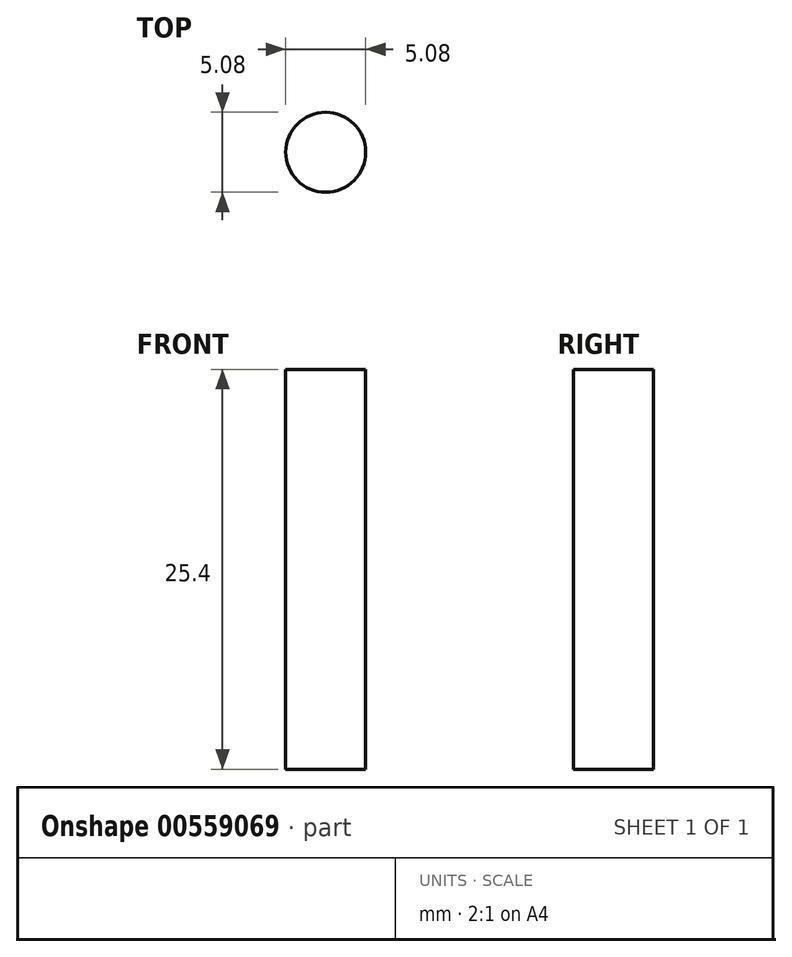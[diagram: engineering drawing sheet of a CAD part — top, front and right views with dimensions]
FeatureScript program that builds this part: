
annotation { "Feature Type Name" : "Feature", "Feature Type Description" : "" }
export const myFeature = defineFeature(function(context is Context, id is Id, definition is map)
    precondition{}
    {
        {
            var Q0;
            Q0=qCreatedBy(makeId("Top.planeOp"),FACE);
            var sketch = newSketch(context, id + "F0", { "sketchPlane" : qUnion([Q0])});
            skCircle(sketch, "E0", {"center": v(-43.44, 31.03) * mm, "radius": 2.54 * mm});
            skSolve(sketch);
        }
        {
            var Q0;
            Q0 = qSketchRegion(id + "F0", true);
            extrude(context, id + "F1", {"entities" : qUnion([Q0]), "depth" : 25.4 * mm, "offsetDistance" : 25.4 * mm});
        }
    });
